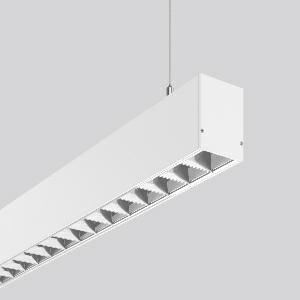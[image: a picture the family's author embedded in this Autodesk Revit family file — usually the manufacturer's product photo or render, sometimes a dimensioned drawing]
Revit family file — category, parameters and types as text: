
# Revit family: less_is_more_50_312341_002_d22c
name_source: partatom
category: Lighting Fixtures
units: mm (PartAtom-declared; Revit-internal decimal feet)

## family parameters
Cut with Voids When Loaded = No
Host = Face
Light Source = No
Part Type = Normal
Room Calculation Point = No
Round Connector Dimension = Use Diameter
Shared = No

## types (1)
- LESS IS MORE 50 (1 x LED Modul 830, 3950 lm, 3000)
    Apparent Load = 35 VA
    CIE Flux Codes = 95 100 100 63 100
    Color Rendering = 80
    Color Temperature = 3000
    Default Elevation = 1800 mm
    Description = Series: LESS IS MORE 50
Linear pendant luminaire for aesthetically sophisticated lighting. Housing: extruded aluminium profile, powder-coated. End cap aluminium powder-coated. Canopy made of aluminium, powder-coated. Alea optical system: Reflector structure (ABS, Aluminium-coated, highly polished) with integrated diffuser made of non-yellowing plastic (PMMA) opal for glare-free light at the workstation (screen-compliant according to EN 12464-1). Direct 65%, indirect 35% light emission. Suitable for pendant. 2-point steel cable suspension freely positionable and infinitely height-adjustable. Special lengths available on request. LED unit with integrated converter interchangeable and removable. Suitable for through-wiring. With sensors or as a safety luminaire on request. 
Colour: traffic white, matt (RAL 9016)
Length: 847 mm
Width: 57 mm
Height: 75 mm
Suspension length: 2000 mm
Lamp: LED
Socket: without socket
Colour temperature: 3000K
Colour rendering index (CRI): 80
Light source: LED
Socket lamp2: Without base
Colour temperature: 3000K
System power: 35 W
Rated luminous flux: 3950 lm
Luminous efficiency: 113 lm/W
Control gear: Regulated power supply
Control gear: Regulated power supply
Protection class: I
Type of protection: IP 20
    Height = 75 mm
    Lamp = 1 x LED Modul 830
    Lamp Light Flux = 3950 lm
    Lamp count = 1
    Length = 847 mm
    Lifetime = 50000 h
    Luminous efficacy = 113 lm/W
    Manufacturer = RZB
    ModVariant = No
    Model = 312341.002
    Mounting Place = Ceiling
    Mounting Type = Pendant
    Number of Poles = 1
    OnlyDefault = Yes
    Power Factor = 1
    Product Name = LESS IS MORE 50
    Product group = Pendant LED linear luminaires
    ProductGroupID = 907
    Protection Class = Protection class I
    Protection Degree = IP 20
    RLX_Detail_Level = 1
    RLX_Emergency_Light_Flux = 0 lm
    RLX_Emergency_Type = 0
    RLX_Emergency_Type_DB = No
    RlxData = <blob elided: 37449 chars, md5=97801d9e>
    Socket = socket
    Standby Power = 0 W
    System Light Flux = 3950 lm
    System Power = 35 W
    Type Comments = Product without accessories
    Type Image = 312342.002.jpg
    URL = http://relux.com
    VarID = ---
    Voltage = 230 V
    Voltage Range = 220-240 V
    Weight = 0.00 kg
    Width = 57 mm

## geometry (parser evidence)
native form markers: Blend x4, Sweep x12
no freeform markers — native parametric forms only
